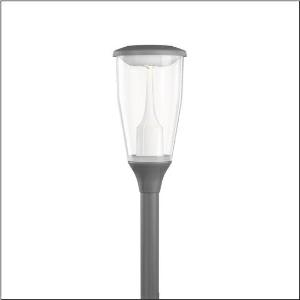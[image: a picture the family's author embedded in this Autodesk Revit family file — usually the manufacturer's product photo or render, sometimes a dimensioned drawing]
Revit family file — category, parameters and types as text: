
# Revit family: dl_11_iq___p1_0a_5xa5565ff14h000022_0ce9
name_source: partatom
category: Lighting Fixtures
units: mm (PartAtom-declared; Revit-internal decimal feet)

## family parameters
Cut with Voids When Loaded = No
Host = Face
Light Source = No
Part Type = Normal
Room Calculation Point = No
Round Connector Dimension = Use Diameter
Shared = No

## types (1)
- --- (1 x LED, 1530 lm, 10.5 W, 3000K)
    Apparent Load = 11 VA
    CIE Flux Codes = 34 63 91 95 100
    Color Rendering = 70
    Color Temperature = 3000K
    Default Elevation = 1800 mm
    Description = DL 11 iQ, mast luminaire, Module 540 iQ-SR, primary light control with 3 zone facetted reflector, of plastic, silver coated, highly specular, structured, primary optical cover: cover, of PMMA, transparent, light distribution: P1.0a, light emission: direct distribution, primary light characteristic: asymmetric, installation type: post-top, LED, High Power LED, rated luminous flux: 1.560lm, luminous efficacy: 149lm/W, light colour: 730, colour temperature: 3000K, control: Street-Remote, Auto-Match, Temp-Guard, Lumen-Switch, Night-Set, Smart-Wire, Light-Fading, Desk-Remote (wireless, voltage-free reading and setting of iQ features in the workshop via application-optimized NFC function/RFID function), optimised constant luminous flux control (CLO 2.0), mains connection: 220..240V, AC, 50/60Hz, connection cable pre-assembled, cable length: 5,5m, start of lifetime: 10W, end of service life: 11W, reduction: 5W, luminaire housing, upper part, of diecast aluminium, coated, Siteco® metallic grey (DB 702S), spigot size: 60mm (post-top), post-top mast mounting element, of diecast aluminium, coated, Siteco® metallic grey (DB 702S), Module 540 iQ-SR, traffic white (RAL 9016), equipment: standard, protection rating (complete): IP66, insulation class (complete): insulation class II (safety insulation), certification: CE, ENEC, ENEC+, VDE, packaging unit: 1 piece

Light Distribution: P1.0a
    Height = 665 mm
    Lamp = 1 x LED
    Lamp Light Flux = 1530 lm
    Lamp Power = 10.5 W
    Lamp count = 1
    Length = 334 mm
    Luminous efficacy = 146 lm/W
    Manufacturer = Siteco
    ModVariant = No
    Model = 5XA5565FF14H000022
    Number of Poles = 1
    OnlyDefault = Yes
    Power Factor = 1
    Product Name = DL 11 iQ | P1.0a
    Product group = mast luminaire | pylon top
    ProductGroupID = 6100
    Protection Class = Protection class II
    Protection Degree = IP 66
    RLX_Detail_Level = 1
    RLX_Emergency_Light_Flux = 0 lm
    RLX_Emergency_Type = 0
    RLX_Emergency_Type_DB = No
    RlxData = <blob elided: 103253 chars, md5=9ba50efa>
    Socket = socket
    Standby Power = 0 W
    System Light Flux = 1530 lm
    System Power = 11 W
    Type Comments = factory setting: luminous flux: 100 % | dim-lin: 254 | 419 mA
    Type Image = l_1258354.jpg
    URL = http://relux.com
    VarID = @adj_042437
    Voltage = 0 V
    Weight = 0.00 kg
    Width = 0 mm  [stored 0 ft]

note: [stored X ft] marks values corroborated as IEEE doubles in the binary element streams (Revit-internal decimal feet)

## geometry (parser evidence)
native form markers: Blend x4, Sweep x11
no freeform markers — native parametric forms only
